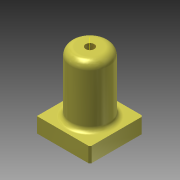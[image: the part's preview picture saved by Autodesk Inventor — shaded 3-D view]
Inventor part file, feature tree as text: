
AUTODESK INVENTOR PART (.ipt)
format: ipt  version: 2013 (Build 170138000, 138)  size: 531,968 bytes
history: native  units: mm
features: sketch x5, fillet x2, other x2, revolve x1, extrude x1, chamfer x1, helix x1
ambient origin geometry x8: Origin, YZ Plane, XZ Plane, XY Plane, X Axis, Y Axis, Z Axis, Center Point
bodies: Solid1 (feature_tree)
feature tree (13):
  revolve  "Revolution1"  [1 undecoded]
  fillet  "Fillet1"  Radius=0.66mm
  extrude  "Extrusion1"  TaperAngle=90.0deg  [1 undecoded]
  chamfer  "Chamfer1"  Distance=5.0mm
  sketch  "Sketch3"  dims[d5=5.0mm]
  sketch  "Sketch4"  dims[d6=5.0mm d8=5.0mm d9=5.0mm d10=5.0mm d11=10.0mm d12=0.0mm d13=1.0mm d14=2.0mm d15=45.0deg d16=7.0mm d17=10.0mm d18=71.5mm d19=0.0mm d20=90.0deg d21=90.0deg d22=0.0mm d23=0.0mm d24=3.0mm]
  other  "Work Axis1"
  fillet  "Fillet2"  Radius=5.0mm
  sketch  "3D Sketch1"
  sketch  "Sketch1"  dims[d0=3.53mm d1=1.09mm d2=0.66mm]
  sketch  "Sketch2"  dims[d3=48.91mm d4=90.0deg]
  other  "Srf1"
  helix  "Coil1"  [1 undecoded]
note: 3 required parameter values undecoded (feature->parameter linkage not recoverable at this tier; creation-order binding heuristic only, values carry confidence <= 0.55)